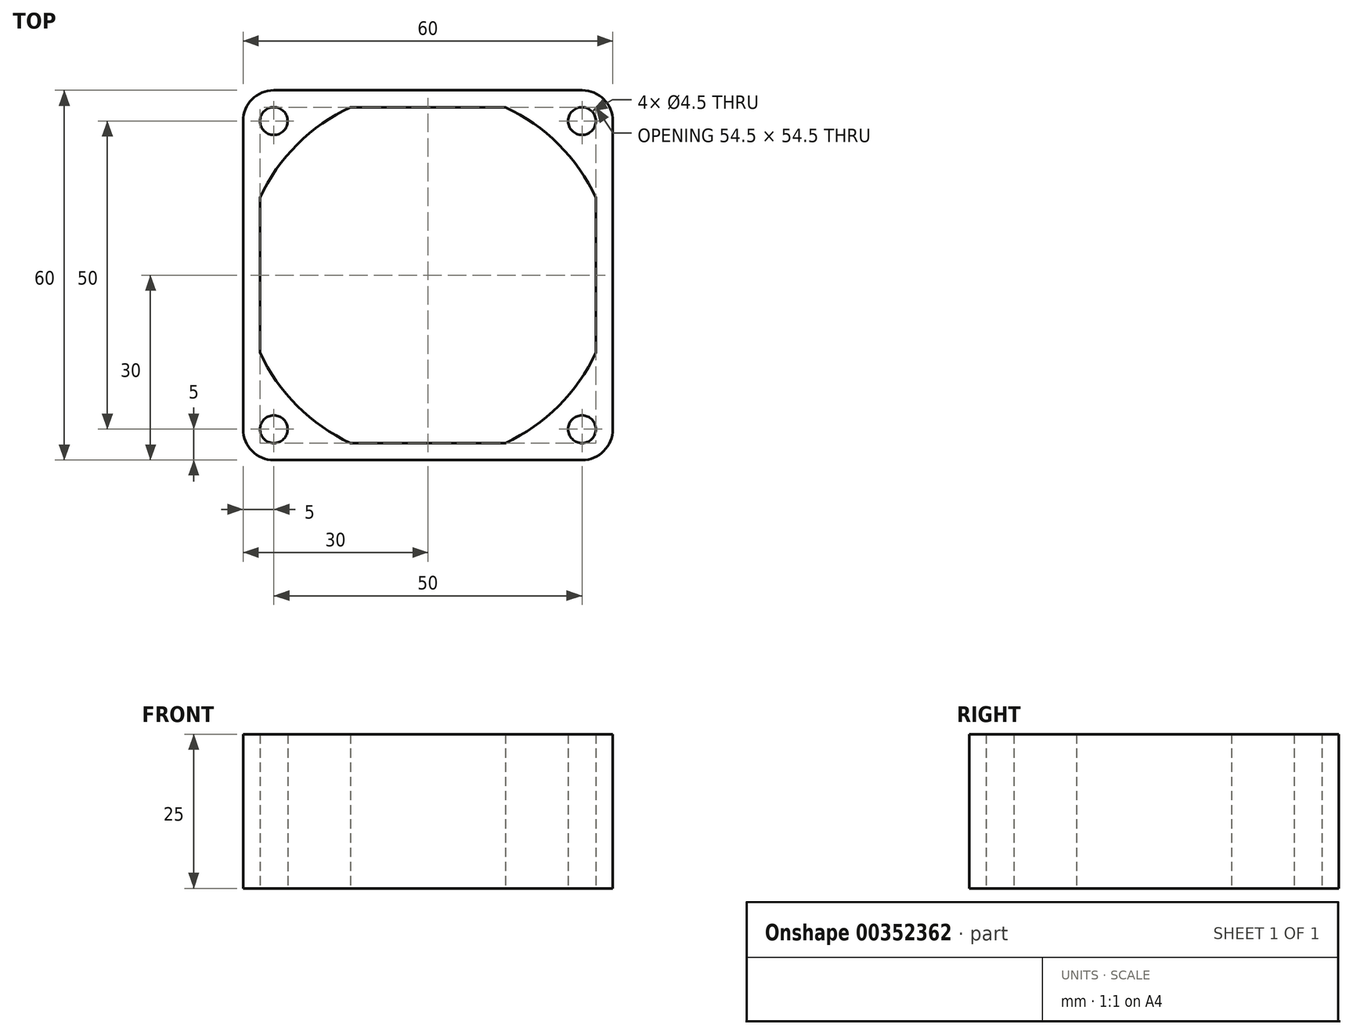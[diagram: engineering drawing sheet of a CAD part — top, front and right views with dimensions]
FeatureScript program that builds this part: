
annotation { "Feature Type Name" : "Feature", "Feature Type Description" : "" }
export const myFeature = defineFeature(function(context is Context, id is Id, definition is map)
    precondition{}
    {
        {
            var Q0;
            Q0=qCreatedBy(makeId("Top.planeOp"),FACE);
            var sketch = newSketch(context, id + "F0", { "sketchPlane" : qUnion([Q0])});
            skLineSegment(sketch, "E0.bottom", {"start": v(-30, 30) * mm, "end": v(30, 30) * mm});
            skLineSegment(sketch, "E0.top", {"start": v(-30, -30) * mm, "end": v(30, -30) * mm});
            skLineSegment(sketch, "E0.left", {"start": v(-30, 30) * mm, "end": v(-30, -30) * mm});
            skLineSegment(sketch, "E0.right", {"start": v(30, 30) * mm, "end": v(30, -30) * mm});
            skCircle(sketch, "E1", {"center": v(-25, 25) * mm, "radius": 2.25 * mm});
            skCircle(sketch, "E2", {"center": v(-25, -25) * mm, "radius": 2.25 * mm});
            skCircle(sketch, "E3", {"center": v(25, 25) * mm, "radius": 2.25 * mm});
            skCircle(sketch, "E4", {"center": v(25, -25) * mm, "radius": 2.25 * mm});
            skCircle(sketch, "E5", {"center": v(0, 0) * mm, "radius": 30 * mm});
            skLineSegment(sketch, "E6", {"start": v(-12.55, 27.25) * mm, "end": v(12.55, 27.25) * mm});
            skLineSegment(sketch, "E7", {"start": v(-12.55, 27.25) * mm, "end": v(-12.55, 30) * mm});
            skLineSegment(sketch, "E8", {"start": v(12.55, 27.25) * mm, "end": v(12.55, 30) * mm});
            skLineSegment(sketch, "E9", {"start": v(-12.55, 30) * mm, "end": v(12.55, 30) * mm});
            skLineSegment(sketch, "E10", {"start": v(-27.25, 12.55) * mm, "end": v(-27.25, -12.55) * mm});
            skLineSegment(sketch, "E11", {"start": v(-27.25, -12.55) * mm, "end": v(-30, -12.55) * mm});
            skLineSegment(sketch, "E12", {"start": v(-30, -12.55) * mm, "end": v(-30, 12.55) * mm});
            skLineSegment(sketch, "E13", {"start": v(-30, 12.55) * mm, "end": v(-27.25, 12.55) * mm});
            skLineSegment(sketch, "E14", {"start": v(-12.55, -27.25) * mm, "end": v(12.55, -27.25) * mm});
            skLineSegment(sketch, "E15", {"start": v(12.55, -27.25) * mm, "end": v(12.55, -30) * mm});
            skLineSegment(sketch, "E16", {"start": v(12.55, -30) * mm, "end": v(-12.55, -30) * mm});
            skLineSegment(sketch, "E17", {"start": v(-12.55, -30) * mm, "end": v(-12.55, -27.25) * mm});
            skLineSegment(sketch, "E18", {"start": v(27.25, -12.55) * mm, "end": v(30, -12.55) * mm});
            skLineSegment(sketch, "E19", {"start": v(27.25, -12.55) * mm, "end": v(27.25, 12.55) * mm});
            skLineSegment(sketch, "E20", {"start": v(27.25, 12.55) * mm, "end": v(30, 12.55) * mm});
            skLineSegment(sketch, "E21", {"start": v(30, 12.55) * mm, "end": v(30, -12.55) * mm});
            skSolve(sketch);
        }
        {
            var Q0;
            Q0 = qSketchRegion(id + "F0", true);
            extrude(context, id + "F1", {"entities" : qUnion([Q0]), "endBound" : BoundingType.SYMMETRIC, "depth" : 25 * mm});
        }
        {
            var Q0;
            Q0=makeQuery(id+"F1.opExtrude","SWEPT_EDGE",EDGE,{"disambiguationData":[OSD([sQuery(id+"F0.wireOp",EDGE,"E0.bottom"),sQuery(id+"F0.wireOp",EDGE,"E0.left")])]});
            var Q1;
            Q1=makeQuery(id+"F1.opExtrude","SWEPT_EDGE",EDGE,{"disambiguationData":[OSD([sQuery(id+"F0.wireOp",EDGE,"E0.top"),sQuery(id+"F0.wireOp",EDGE,"E0.right")])]});
            var Q2;
            Q2=makeQuery(id+"F1.opExtrude","SWEPT_EDGE",EDGE,{"disambiguationData":[OSD([sQuery(id+"F0.wireOp",EDGE,"E0.bottom"),sQuery(id+"F0.wireOp",EDGE,"E0.right")])]});
            var Q3;
            Q3=makeQuery(id+"F1.opExtrude","SWEPT_EDGE",EDGE,{"disambiguationData":[OSD([sQuery(id+"F0.wireOp",EDGE,"E0.top"),sQuery(id+"F0.wireOp",EDGE,"E0.left")])]});
            fillet(context, id + "F2", {"entities" : qUnion([Q0, Q1, Q2, Q3]), "radius" : 5 * mm, "tangentPropagation" : true, "allowEdgeOverflow" : false});
        }
    });
